# Revit family: Zumtobel MIREL-L mini EM
name_source: partatom
category: Lighting Fixtures
revit_build: Autodesk Revit 2014 (Build: 20140709_2115(x64)
units: mm (PartAtom-declared; Revit-internal decimal feet)

## types (1)
- MIREL-L mini EM LED1000-830 LDE
    Apparent Load = 10 VA
    Assembly Code = D5020200
    Color Filter = 16777215
    Default Elevation = 0 mm  [stored 0 ft]
    Description = Recessed LED luminaire
    Dimming Lamp Color Temperature Shift = <None>
    Emit Shape Visible in Rendering = No
    Emit from Rectangle Length = 168 mm  [stored 0.551181 ft]
    Emit from Rectangle Width = 168 mm  [stored 0.551181 ft]
    Height = 38 mm  [stored 0.124672 ft]
    Lamp = LED
    Length = 150 mm
    Manufacturer = Zumtobel Lighting
    Model = 42184006
    Photometric Web File = 42184006_(STD).IES
    Tilt Angle = 90.00°
    URL = http://www.zumtobel.com
    Voltage = 230 V
    Width = 150 mm

note: [stored X ft] marks values corroborated as IEEE doubles in the binary element streams (Revit-internal decimal feet)

## geometry (parser evidence)
native form markers: Sweep x3
no freeform markers — native parametric forms only
